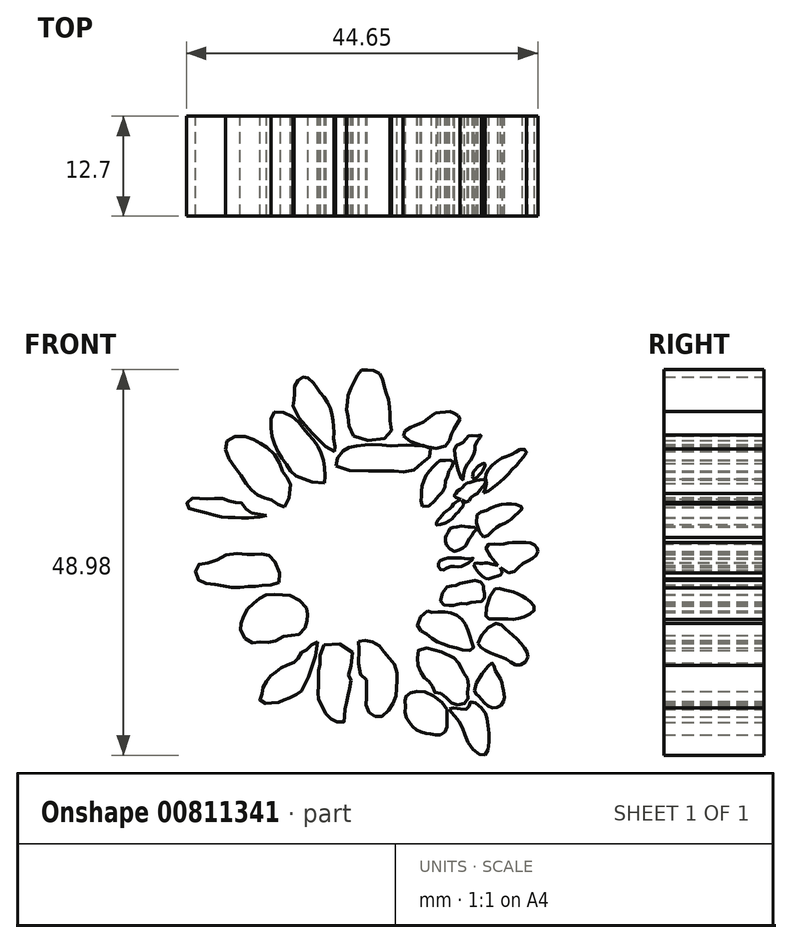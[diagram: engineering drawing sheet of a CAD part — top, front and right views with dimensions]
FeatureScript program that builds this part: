
annotation { "Feature Type Name" : "Feature", "Feature Type Description" : "" }
export const myFeature = defineFeature(function(context is Context, id is Id, definition is map)
    precondition{}
    {
        {
            var Q0;
            Q0=qCreatedBy(makeId("Front.planeOp"), FACE);
            var sketch = newSketch(context, id + "F0", { "sketchPlane" : qUnion([Q0])});
            skFitSpline(sketch, "E0", {"points": [v(7.13, 6.1) * mm, v(6.9, 6.81) * mm, v(7, 7.39) * mm, v(7, 7.93) * mm, v(7.03, 8.63) * mm, v(7.29, 9.37) * mm, v(7.5, 9.97) * mm, v(7.96, 10.58) * mm, v(8.4, 11.13) * mm, v(8.88, 11.54) * mm, v(9.27, 11.92) * mm, v(9.81, 11.92) * mm, v(10.39, 11.96) * mm, v(11, 11.92) * mm, v(11, 11.35) * mm, v(10.6, 10.9) * mm, v(10.42, 10.4) * mm, v(10.23, 9.75) * mm, v(9.97, 9.14) * mm, v(9.94, 8.35) * mm, v(9.4, 7.7) * mm, v(8.95, 7.23) * mm, v(8.18, 6.3) * mm, v(7.13, 6.1) * mm]});
            skFitSpline(sketch, "E1", {"points": [v(11.12, 7.42) * mm, v(11.38, 7.7) * mm, v(11.6, 8.12) * mm, v(12.05, 8.38) * mm, v(12.4, 8.8) * mm, v(12.85, 9.08) * mm, v(13.3, 9.2) * mm, v(13.74, 9.34) * mm, v(14.48, 9.46) * mm, v(15.12, 9.5) * mm, v(15.05, 8.98) * mm, v(14.57, 8.4) * mm, v(14.06, 7.7) * mm, v(13.36, 7.32) * mm, v(12.85, 6.65) * mm, v(11.98, 6.97) * mm, v(11.12, 7.42) * mm]});
            skFitSpline(sketch, "E2", {"points": [v(8.85, 3.78) * mm, v(9.04, 4.29) * mm, v(9.4, 4.7) * mm, v(9.78, 5.21) * mm, v(10.26, 5.56) * mm, v(10.83, 6.1) * mm, v(11.12, 6.46) * mm, v(11.57, 6.75) * mm, v(11.98, 6.97) * mm, v(12.37, 6.43) * mm, v(11.98, 5.82) * mm, v(11.57, 5.3) * mm, v(11.12, 4.86) * mm, v(10.67, 4.35) * mm, v(9.71, 3.9) * mm, v(8.85, 3.78) * mm]});
            skFitSpline(sketch, "E3", {"points": [v(10.16, 1.19) * mm, v(10.07, 1.86) * mm, v(10.1, 2.37) * mm, v(10.35, 2.75) * mm, v(10.64, 3.3) * mm, v(11.12, 3.42) * mm, v(11.98, 3.58) * mm, v(12.46, 3.58) * mm, v(13, 3.49) * mm, v(13.36, 3.49) * mm, v(14, 3.3) * mm, v(13.61, 2.85) * mm, v(13.36, 2.34) * mm, v(12.91, 1.73) * mm, v(12.62, 1.15) * mm, v(11.98, 0.7) * mm, v(11.12, 0.42) * mm, v(10.16, 1.19) * mm]});
            skFitSpline(sketch, "E4", {"points": [v(9.15, -1.06) * mm, v(10.1, -0.5) * mm, v(11.12, -0.45) * mm, v(12.06, -0.45) * mm, v(12.95, -0.56) * mm, v(13.57, -0.5) * mm, v(12.78, -1.17) * mm, v(11.72, -1.57) * mm, v(10.66, -1.57) * mm, v(9.48, -1.96) * mm, v(9.15, -1.06) * mm]});
            skFitSpline(sketch, "E5", {"points": [v(10.21, -4.14) * mm, v(11.12, -4.03) * mm, v(11.83, -3.7) * mm, v(12.84, -3.52) * mm, v(13.9, -3.3) * mm, v(14.85, -3.86) * mm, v(14.85, -4.47) * mm, v(15.02, -5.15) * mm, v(14.68, -5.93) * mm, v(13.62, -6.04) * mm, v(12.78, -6.26) * mm, v(11.78, -6.26) * mm, v(11.12, -6.49) * mm, v(10.43, -6.49) * mm, v(9.48, -6.1) * mm, v(10.21, -4.14) * mm]});
            skFitSpline(sketch, "E6", {"points": [v(7.75, -7.16) * mm, v(8.3, -7.33) * mm, v(9.15, -7.33) * mm, v(10.21, -7.33) * mm, v(11.12, -7.55) * mm, v(11.94, -8.05) * mm, v(12.56, -8.84) * mm, v(12.9, -9.68) * mm, v(13.23, -10.57) * mm, v(13.4, -11.19) * mm, v(13.57, -12.02) * mm, v(12.61, -12.2) * mm, v(11.6, -11.91) * mm, v(10.43, -11.63) * mm, v(9.48, -11.3) * mm, v(8.64, -10.96) * mm, v(7.75, -10.18) * mm, v(6.91, -9.68) * mm, v(6.46, -8.78) * mm, v(7.75, -7.16) * mm]});
            skFitSpline(sketch, "E7", {"points": [v(11.12, -13.14) * mm, v(11.78, -13.93) * mm, v(12.17, -14.65) * mm, v(12.56, -15.32) * mm, v(12.95, -16.22) * mm, v(12.84, -17.45) * mm, v(12.9, -18.34) * mm, v(12.28, -19.01) * mm, v(11.12, -19.01) * mm, v(10.43, -18.51) * mm, v(9.48, -17.67) * mm, v(8.64, -17.5) * mm, v(8.3, -16.55) * mm, v(7.75, -16) * mm, v(7.13, -15.32) * mm, v(6.63, -14.26) * mm, v(6.46, -12.92) * mm, v(6.97, -11.91) * mm, v(11.12, -13.14) * mm]});
            skFitSpline(sketch, "E8", {"points": [v(10.21, -19.69) * mm, v(10.21, -20.86) * mm, v(10.21, -22.1) * mm, v(9.48, -22.87) * mm, v(8.64, -22.87) * mm, v(7.75, -22.76) * mm, v(6.97, -22.54) * mm, v(6.07, -22.1) * mm, v(5.51, -21.42) * mm, v(4.95, -20.47) * mm, v(4.95, -19.18) * mm, v(4.95, -18.18) * mm, v(5.74, -17.56) * mm, v(7.75, -17.56) * mm, v(10.21, -19.69) * mm]});
            skFitSpline(sketch, "E9", {"points": [v(-0.98, -11.02) * mm, v(-0.86, -11.07) * mm, v(0, -10.9) * mm, v(0.65, -11.07) * mm, v(1.37, -11.4) * mm, v(2.04, -12.08) * mm, v(2.38, -12.58) * mm, v(3.05, -13.37) * mm, v(3.55, -13.93) * mm, v(3.9, -14.88) * mm, v(3.9, -15.55) * mm, v(3.9, -16.39) * mm, v(3.78, -17.23) * mm, v(3.72, -18) * mm, v(3.44, -18.8) * mm, v(3, -19.52) * mm, v(2.32, -20.36) * mm, v(1.7, -20.64) * mm, v(1.04, -20.52) * mm, v(0.48, -20.25) * mm, v(0, -19.46) * mm, v(0, -18.68) * mm, v(0, -17.9) * mm, v(0, -16.89) * mm, v(0, -15.94) * mm, v(-0.7, -15.35) * mm, v(-0.98, -13.98) * mm, v(-0.98, -11.6) * mm, v(-0.98, -11.02) * mm]});
            skFitSpline(sketch, "E10", {"points": [v(-1.8, -12.41) * mm, v(-2.3, -15.2) * mm, v(-2.04, -15.6) * mm, v(-2.1, -16.9) * mm, v(-2.32, -17.67) * mm, v(-2.48, -18.79) * mm, v(-2.71, -19.52) * mm, v(-2.76, -20.47) * mm, v(-2.8, -21.22) * mm, v(-3.5, -21.32) * mm, v(-4.34, -20.98) * mm, v(-5.12, -20.3) * mm, v(-5.56, -19.4) * mm, v(-6.13, -18.24) * mm, v(-6.12, -17.29) * mm, v(-6.06, -16.54) * mm, v(-6.07, -15.35) * mm, v(-6.06, -14.34) * mm, v(-5.86, -13.75) * mm, v(-5.48, -11.6) * mm, v(-1.8, -12.41) * mm]});
            skFitSpline(sketch, "E11", {"points": [v(-6.23, -11.13) * mm, v(-7.02, -11.52) * mm, v(-7.63, -12.14) * mm, v(-8.19, -12.42) * mm, v(-8.7, -13.2) * mm, v(-9.14, -13.65) * mm, v(-9.98, -13.98) * mm, v(-10.82, -14.43) * mm, v(-11.49, -14.93) * mm, v(-12.22, -15.5) * mm, v(-12.78, -16.22) * mm, v(-13.17, -17) * mm, v(-13.28, -17.9) * mm, v(-13.5, -18.57) * mm, v(-12.66, -18.96) * mm, v(-11.94, -18.85) * mm, v(-11.04, -18.8) * mm, v(-10.43, -18.46) * mm, v(-9.7, -18.23) * mm, v(-8.7, -17.67) * mm, v(-8.08, -17.11) * mm, v(-6.23, -11.13) * mm]});
            skFitSpline(sketch, "E12", {"points": [v(-7.58, -6.8) * mm, v(-7.48, -7.87) * mm, v(-7.63, -8.94) * mm, v(-8.7, -10.22) * mm, v(-10.23, -10.31) * mm, v(-11.89, -11.13) * mm, v(-13.36, -11.13) * mm, v(-14.82, -11.13) * mm, v(-16, -9.53) * mm, v(-15.8, -8.45) * mm, v(-15.12, -6.99) * mm, v(-13.94, -5.9) * mm, v(-12.77, -5.13) * mm, v(-11.1, -5.13) * mm, v(-9.74, -5.22) * mm, v(-7.58, -6.8) * mm]});
            skFitSpline(sketch, "E13", {"points": [v(-11.1, -3.56) * mm, v(-12.77, -3.85) * mm, v(-13.94, -4.05) * mm, v(-15.12, -4.05) * mm, v(-16.78, -4.25) * mm, v(-18.25, -3.95) * mm, v(-20.01, -3.76) * mm, v(-21.48, -3.07) * mm, v(-21.48, -1.4) * mm, v(-19.72, -1.02) * mm, v(-17.66, 0) * mm, v(-15.12, 0) * mm, v(-13.94, 0) * mm, v(-12.77, 0) * mm, v(-11.49, -1.11) * mm, v(-11.1, -3.56) * mm]});
            skFitSpline(sketch, "E14", {"points": [v(-11.49, 1.04) * mm, v(-12.66, 1.43) * mm, v(-13.94, 1.04) * mm, v(-15.12, 1.43) * mm, v(-16.3, 1.23) * mm, v(-17.66, 1.04) * mm, v(-19.03, 2.21) * mm, v(-17.66, 3.58) * mm, v(-16.49, 3.58) * mm, v(-15.12, 4.17) * mm], "startDerivative": vector(-11.1, 6.33) * mm, "endDerivative": vector(12.42, 7.25) * mm});
            skFitSpline(sketch, "E15", {"points": [v(-15.12, 4.17) * mm, v(-13.94, 4.17) * mm, v(-11.87, 4.17) * mm, v(-10.43, 3.58) * mm, v(-11.87, 1.26) * mm], "startDerivative": vector(5.49, -0.1) * mm, "endDerivative": vector(-7.91, -8.96) * mm});
            skFitSpline(sketch, "E16", {"points": [v(-10.43, 6.03) * mm, v(-11.49, 6.62) * mm, v(-12.66, 7.1) * mm, v(-13.94, 7.6) * mm, v(-15.12, 8.77) * mm, v(-16.3, 10.53) * mm, v(-17.66, 12.59) * mm, v(-17.66, 14.45) * mm, v(-15.6, 15.03) * mm, v(-13.94, 14.35) * mm, v(-12.66, 13.66) * mm, v(-11.1, 11.8) * mm, v(-10.43, 10.14) * mm, v(-9.7, 9.06) * mm, v(-10.43, 6.03) * mm]});
            skFitSpline(sketch, "E17", {"points": [v(-5.3, 9.06) * mm, v(-5.3, 10.14) * mm, v(-5.3, 11.4) * mm, v(-5.61, 12.45) * mm, v(-6.04, 13.5) * mm, v(-6.66, 14.42) * mm, v(-7.47, 15.4) * mm, v(-8.14, 16.21) * mm, v(-9, 17.2) * mm, v(-10.43, 18) * mm, v(-11.85, 18) * mm, v(-12.1, 16.64) * mm, v(-12.03, 15.1) * mm, v(-11.6, 13.87) * mm, v(-10.98, 12.57) * mm, v(-10.43, 11.8) * mm, v(-9.7, 10.78) * mm, v(-9.2, 10.14) * mm, v(-5.3, 9.06) * mm]});
            skFitSpline(sketch, "E18", {"points": [v(-12.66, 4.97) * mm, v(-13.95, 5.16) * mm, v(-15.25, 5.72) * mm, v(-15.99, 6.62) * mm, v(-16.97, 6.62) * mm, v(-18.15, 7.1) * mm, v(-19.63, 7.1) * mm, v(-20.99, 7.1) * mm, v(-22.22, 7.1) * mm, v(-22.84, 6.09) * mm, v(-21.05, 5.47) * mm, v(-19.7, 5.1) * mm, v(-18.15, 4.73) * mm, v(-17.1, 4.67) * mm, v(-16.05, 4.67) * mm, v(-14.75, 4.67) * mm, v(-12.66, 4.97) * mm]});
            skFitSpline(sketch, "E19", {"points": [v(-4.07, 13.06) * mm, v(-4.13, 14.3) * mm, v(-4.13, 15.47) * mm, v(-4.25, 16.64) * mm, v(-4.32, 17.57) * mm, v(-4.69, 18.8) * mm, v(-5.3, 19.92) * mm, v(-6.04, 20.78) * mm, v(-6.54, 21.58) * mm, v(-7.65, 22.51) * mm, v(-8.33, 22.39) * mm, v(-9.13, 21.34) * mm, v(-9.13, 19.86) * mm, v(-9.26, 18.56) * mm, v(-4.07, 13.06) * mm]});
            skFitSpline(sketch, "E20", {"points": [v(-3.88, 11.23) * mm, v(-3.57, 12.4) * mm, v(-2.89, 13.2) * mm, v(-2.15, 13.58) * mm, v(-1.22, 13.76) * mm, v(0, 13.95) * mm, v(0.82, 13.95) * mm, v(2.42, 13.89) * mm, v(3.47, 13.76) * mm, v(4.46, 13.89) * mm, v(5.7, 13.89) * mm, v(6.62, 13.82) * mm, v(7.98, 13.7) * mm, v(8.17, 12.65) * mm, v(7.18, 11.72) * mm, v(5.63, 10.58) * mm, v(3.84, 10.58) * mm, v(2.8, 10.58) * mm, v(1.74, 10.58) * mm, v(0.45, 10.58) * mm, v(-3.88, 11.23) * mm]});
            skSolve(sketch);
        }
        {
            var Q0;
            Q0 = qSketchRegion(id + "F0", true);
            extrude(context, id + "F1", {"entities" : qUnion([Q0]), "depth" : 12.7 * mm, "offsetDistance" : 25.4 * mm});
        }
        {
            var Q0;
            Q0=qCreatedBy(makeId("Front.planeOp"), FACE);
            var sketch = newSketch(context, id + "F2", { "sketchPlane" : qUnion([Q0])});
            skFitSpline(sketch, "E21", {"points": [v(-1.65, 15.06) * mm, v(-2.27, 17.22) * mm, v(-2.52, 18.33) * mm, v(-2.4, 19.57) * mm, v(-2.27, 20.5) * mm, v(-1.65, 21.73) * mm, v(-1.22, 22.65) * mm, v(-0.66, 23.4) * mm, v(0, 23.46) * mm, v(0.88, 23.4) * mm, v(1.62, 23.03) * mm, v(2.05, 22.28) * mm, v(2.24, 21.3) * mm, v(2.6, 20.25) * mm, v(2.92, 19.01) * mm, v(2.98, 17.96) * mm, v(2.98, 17.04) * mm, v(2.92, 15.12) * mm, v(-1.65, 15.06) * mm]});
            skFitSpline(sketch, "E22", {"points": [v(4.7, 15.06) * mm, v(5.39, 16.05) * mm, v(6.31, 16.42) * mm, v(7.12, 16.79) * mm, v(8.1, 17.47) * mm, v(8.78, 17.96) * mm, v(9.65, 18.09) * mm, v(10.57, 18.15) * mm, v(11.13, 17.9) * mm, v(11.87, 17.4) * mm, v(11.32, 16.3) * mm, v(10.76, 15.12) * mm, v(9.65, 13.58) * mm, v(4.7, 15.06) * mm]});
            skFitSpline(sketch, "E23", {"points": [v(11.2, 13.27) * mm, v(11.75, 14) * mm, v(12.36, 14.32) * mm, v(12.98, 15.06) * mm, v(13.85, 15.06) * mm, v(14.59, 15.12) * mm, v(13.97, 14.26) * mm, v(13.79, 13.33) * mm, v(13.6, 12.59) * mm, v(13.1, 11.79) * mm, v(12.43, 10.68) * mm, v(12.18, 9.44) * mm, v(11.2, 13.27) * mm]});
            skFitSpline(sketch, "E24", {"points": [v(15.08, 11.48) * mm, v(13.72, 9.63) * mm, v(13.72, 10.68) * mm, v(15.08, 11.48) * mm]});
            skFitSpline(sketch, "E25", {"points": [v(14.87, 7.79) * mm, v(15.2, 8.62) * mm, v(15.1, 9.69) * mm, v(15.32, 10.53) * mm, v(16.15, 11.48) * mm, v(17.22, 12.26) * mm, v(18.06, 12.54) * mm, v(18.95, 12.99) * mm, v(19.68, 13.38) * mm, v(20.35, 13.15) * mm, v(19.9, 12.32) * mm, v(19.17, 11.48) * mm, v(18.22, 10.47) * mm, v(17.16, 9.35) * mm, v(14.87, 7.79) * mm]});
            skFitSpline(sketch, "E26", {"points": [v(14.87, 2.2) * mm, v(16.04, 3.03) * mm, v(17, 3.7) * mm, v(17.78, 4.1) * mm, v(18.4, 4.49) * mm, v(19.23, 5.27) * mm, v(19.79, 5.94) * mm, v(18.84, 6.39) * mm, v(17.78, 6.39) * mm, v(16.38, 6.16) * mm, v(15.2, 5.55) * mm, v(14.03, 4.93) * mm, v(14.87, 2.2) * mm]});
            skFitSpline(sketch, "E27", {"points": [v(15.2, 1.02) * mm, v(16.55, 1.3) * mm, v(17.5, 1.35) * mm, v(18.4, 1.52) * mm, v(19.4, 1.52) * mm, v(20.3, 1.52) * mm, v(21.24, 1.3) * mm, v(21.75, 0.68) * mm, v(21.64, 0) * mm, v(20.74, -0.71) * mm, v(19.45, -1.5) * mm, v(18.11, -2.34) * mm, v(15.2, 1.02) * mm]});
            skFitSpline(sketch, "E28", {"points": [v(13.7, -1.27) * mm, v(14.2, -1.1) * mm, v(14.87, -1.1) * mm, v(15.6, -1.1) * mm, v(15.99, -1.27) * mm, v(16.73, -1.4) * mm, v(17.03, -1.68) * mm, v(17.16, -2.45) * mm, v(16.15, -2.9) * mm, v(15.08, -3) * mm, v(13.7, -1.27) * mm]});
            skFitSpline(sketch, "E29", {"points": [v(16.32, -4.4) * mm, v(17.27, -4.4) * mm, v(18.17, -4.63) * mm, v(19.12, -4.97) * mm, v(19.9, -5.36) * mm, v(20.8, -5.97) * mm, v(21.36, -6.98) * mm, v(20.3, -7.82) * mm, v(18.9, -8.2) * mm, v(17.83, -8.2) * mm, v(17, -8.2) * mm, v(15.93, -8.2) * mm, v(15.2, -7.93) * mm, v(16.32, -4.4) * mm]});
            skFitSpline(sketch, "E30", {"points": [v(14.2, -11.28) * mm, v(14.87, -12.01) * mm, v(15.93, -12.63) * mm, v(17.16, -13.02) * mm, v(18.17, -13.58) * mm, v(19.23, -14.08) * mm, v(20.3, -13.52) * mm, v(20.46, -12.52) * mm, v(19.9, -11.68) * mm, v(19.06, -10.67) * mm, v(18.17, -9.89) * mm, v(17.5, -9.27) * mm, v(16.32, -8.77) * mm, v(14.2, -11.28) * mm]});
            skFitSpline(sketch, "E31", {"points": [v(13.7, -17.27) * mm, v(14.2, -17.94) * mm, v(14.87, -18.72) * mm, v(15.93, -19.45) * mm, v(17, -19.23) * mm, v(17.55, -18.16) * mm, v(17.44, -17.55) * mm, v(17.27, -16.65) * mm, v(17, -15.76) * mm, v(16.32, -14.53) * mm, v(15.93, -13.8) * mm, v(13.7, -17.27) * mm]});
            skFitSpline(sketch, "E32", {"points": [v(10.55, -19.63) * mm, v(11.78, -19.57) * mm, v(12.9, -19.52) * mm, v(13.24, -18.72) * mm, v(14.87, -19.74) * mm, v(15.36, -21.14) * mm, v(15.59, -23.94) * mm, v(14.87, -25.5) * mm, v(13.01, -24.05) * mm, v(12, -21.64) * mm, v(10.89, -20.19) * mm, v(10.55, -19.63) * mm]});
            skSolve(sketch);
        }
        {
            var Q0;
            Q0 = qSketchRegion(id + "F2", true);
            extrude(context, id + "F3", {"entities" : qUnion([Q0]), "depth" : 12.7 * mm, "offsetDistance" : 25.4 * mm});
        }
    });
